# Revit family: NaughtOne_HatchSingleSeatBenchLounge
name_source: partatom
category: Furniture
units: mm (PartAtom-declared; Revit-internal decimal feet)

## family parameters
Always vertical = Yes
Cut with Voids When Loaded = No
Enable Cutting in Views = No
Render Appearance Source = Family Geometry
Room Calculation Point = No
Shared = Yes
Work Plane-Based = No

## types (1)
- Lounge height 16 inch seat height Single Fabric
    Assembly Code = E2020200
    AssetType = Movable
    BIMObjectName = Naughtone_Seating_Hatch_Bench
    Category = Pr_40_50_12_85: Stools
    CodePerformance = PASSED BSEN 16139
    Color = Various
    Default Elevation = 0 mm  [stored 0 ft]
    Description = Hatch Single Seat Bench lounge height 16 inch seat height Single Fabric
    DurationUnit = year
    Export Type to IFC As = IfcFurnishingElementType
    Finish = Upholstered
    IfcExportAs = IfcFurnishingElementType
    IfcExportType = STOOL
    Is2Seat = No
    Is3Seat = No
    IsChair = No
    Keynote = Pr_40_50_12_85
    LeftOffset = 255 mm  [stored 0.836614 ft]
    MainColor = Various
    Manufacturer = naughtone
    ManufacturerAddressUK = naughtone, Knaresborough Tech Park, Manse Lane, Knaresborough, HG5 8LF
    ManufacturerName = Naughtone
    ManufacturerURL = www.naughtone.com
    Material = Fabric, leather/steel/solid wood/beech ply/foam
    Model = NOHAN110L1
    ModelNumber = HAT1ST
    ModelReference = Hatch Single Stool
    NBSDescription = Seating
    NBSReference = 45-35-72/352
    Name = Seating_Hatch_Bench_Naughtone
    NominalHeight = 410 mm  [stored 1.34514 ft]
    NominalLength = 510 mm  [stored 1.67323 ft]
    NominalWidth = 510 mm  [stored 1.67323 ft]
    Package Qty = 1
    ProductInformation = www.naughtone.com/portfolio-view/hatch
    RightOffset = 255 mm  [stored 0.836614 ft]
    Shape = Square
    Size = 510x510x410mm
    SustainabilityPerformance = FSC certified. FISP certified. ISO 14001 certified
    Type IFC Predefined Type = STOOL
    URL = http://www.hermanmiller.com
    Uniclass2015Description = Stools
    Uniclass2015Reference = Pr_40_50_12_85
    Uniclass2015Version = Products v1.5
    Version = 1
    VoidOffset2Seat = 10 mm  [stored 0.0328084 ft]
    VoidOffset3Seat = 10 mm  [stored 0.0328084 ft]
    VoidOffsetCentre = 255 mm  [stored 0.836614 ft]
    WarrantyDurationLabor = 5
    WarrantyDurationParts = 5
    WarrantyDurationUnit = year

note: [stored X ft] marks values corroborated as IEEE doubles in the binary element streams (Revit-internal decimal feet)

## geometry (parser evidence)
native form markers: Sweep x4
no freeform markers — native parametric forms only
